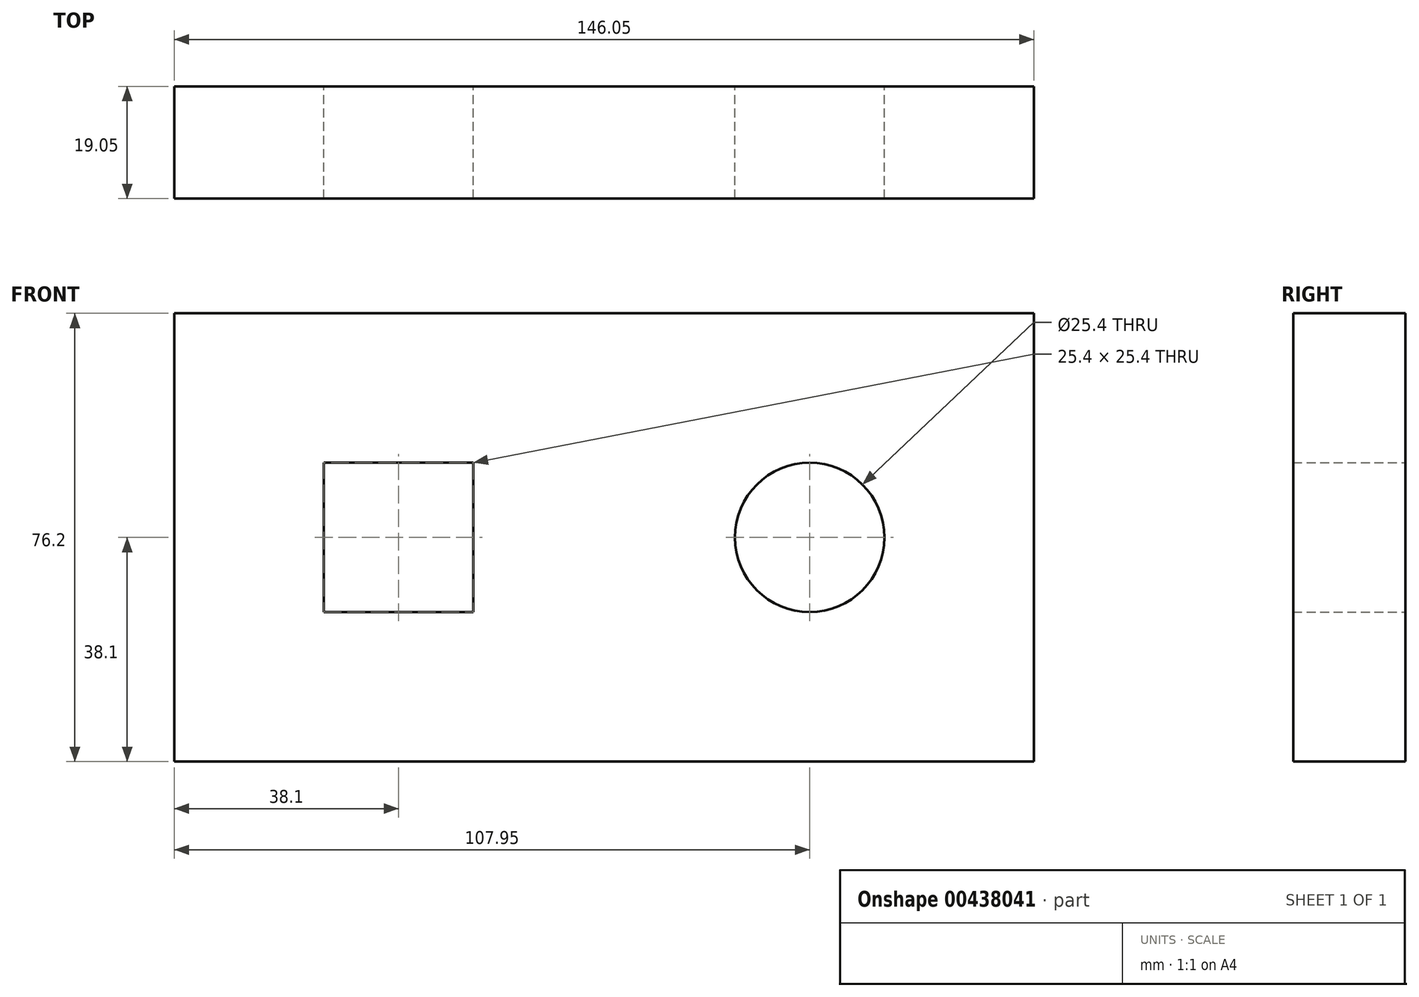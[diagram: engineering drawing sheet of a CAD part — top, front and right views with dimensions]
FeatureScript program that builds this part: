
annotation { "Feature Type Name" : "Feature", "Feature Type Description" : "" }
export const myFeature = defineFeature(function(context is Context, id is Id, definition is map)
    precondition{}
    {
        {
            var Q0;
            Q0=qCreatedBy(makeId("Front.planeOp"),FACE);
            var sketch = newSketch(context, id + "F0", { "sketchPlane" : qUnion([Q0])});
            skLineSegment(sketch, "E0", {"start": v(0, 0) * mm, "end": v(-146.05, 0) * mm});
            skLineSegment(sketch, "E1", {"start": v(-146.05, 0) * mm, "end": v(-146.05, 76.2) * mm});
            skLineSegment(sketch, "E2", {"start": v(-146.05, 76.2) * mm, "end": v(0, 76.2) * mm});
            skLineSegment(sketch, "E3", {"start": v(0, 76.2) * mm, "end": v(0, 0) * mm});
            skCircle(sketch, "E4", {"center": v(-38.1, 38.1) * mm, "radius": 12.7 * mm});
            skPoint(sketch, "E4.centerSnap0", {"position": v(0, 38.1) * mm});
            skLineSegment(sketch, "E5.bottom", {"start": v(-120.65, 50.8) * mm, "end": v(-95.25, 50.8) * mm});
            skLineSegment(sketch, "E5.top", {"start": v(-120.65, 25.4) * mm, "end": v(-95.25, 25.4) * mm});
            skLineSegment(sketch, "E5.left", {"start": v(-120.65, 50.8) * mm, "end": v(-120.65, 25.4) * mm});
            skLineSegment(sketch, "E5.right", {"start": v(-95.25, 50.8) * mm, "end": v(-95.25, 25.4) * mm});
            skSolve(sketch);
        }
        {
            var Q0;
            Q0=makeQuery(id+"F0.imprint","IMPRINT",FACE,{"disambiguationData":[TD([[makeQuery(id+"F0.imprint","IMPRINT",EDGE,{"derivedFrom":sQuery(id+"F0.wireOp",EDGE,"E0")}),-1.0]])]});
            extrude(context, id + "F1", {"entities" : qUnion([Q0]), "depth" : 19.05 * mm});
        }
    });
